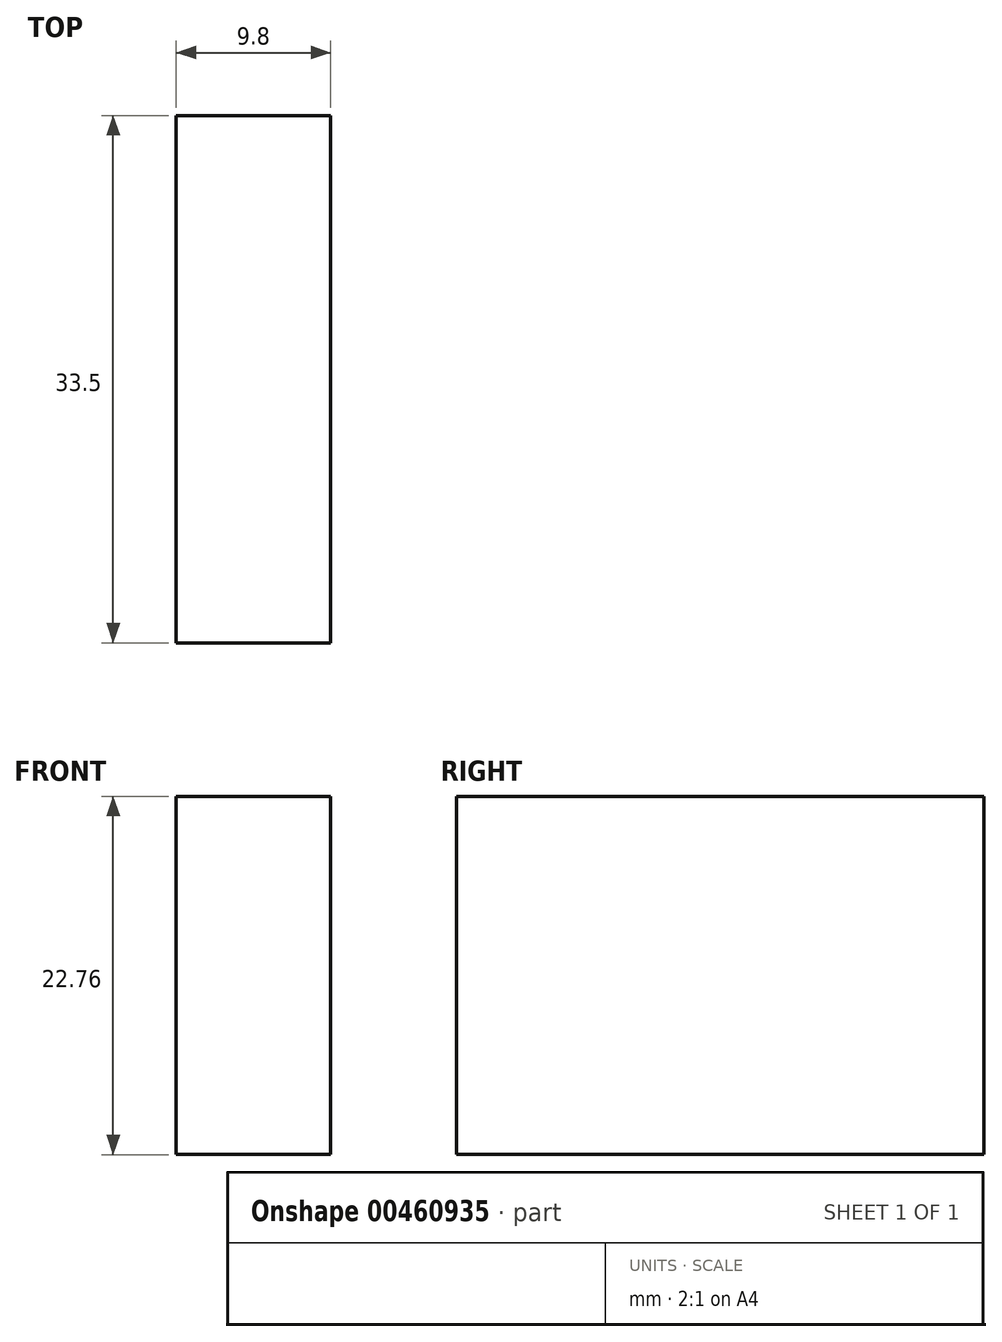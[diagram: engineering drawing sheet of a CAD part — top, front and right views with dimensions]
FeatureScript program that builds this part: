
annotation { "Feature Type Name" : "Feature", "Feature Type Description" : "" }
export const myFeature = defineFeature(function(context is Context, id is Id, definition is map)
    precondition{}
    {
        {
            var Q0;
            Q0=qCreatedBy(makeId("Right.planeOp"),FACE);
            var sketch = newSketch(context, id + "F0", { "sketchPlane" : qUnion([Q0])});
            skLineSegment(sketch, "E0.bottom", {"start": v(16.75, 11.38) * mm, "end": v(-16.75, 11.38) * mm});
            skLineSegment(sketch, "E0.top", {"start": v(16.75, -11.38) * mm, "end": v(-16.75, -11.38) * mm});
            skLineSegment(sketch, "E0.left", {"start": v(16.75, 11.38) * mm, "end": v(16.75, -11.38) * mm});
            skLineSegment(sketch, "E0.right", {"start": v(-16.75, 11.38) * mm, "end": v(-16.75, -11.38) * mm});
            skPoint(sketch, "E0.middle", {"position": v(0, 0) * mm});
            skSolve(sketch);
        }
        {
            var Q0;
            Q0 = qSketchRegion(id + "F0", true);
            extrude(context, id + "F1", {"entities" : qUnion([Q0]), "depth" : 9.8 * mm, "offsetDistance" : 25 * mm});
        }
    });
